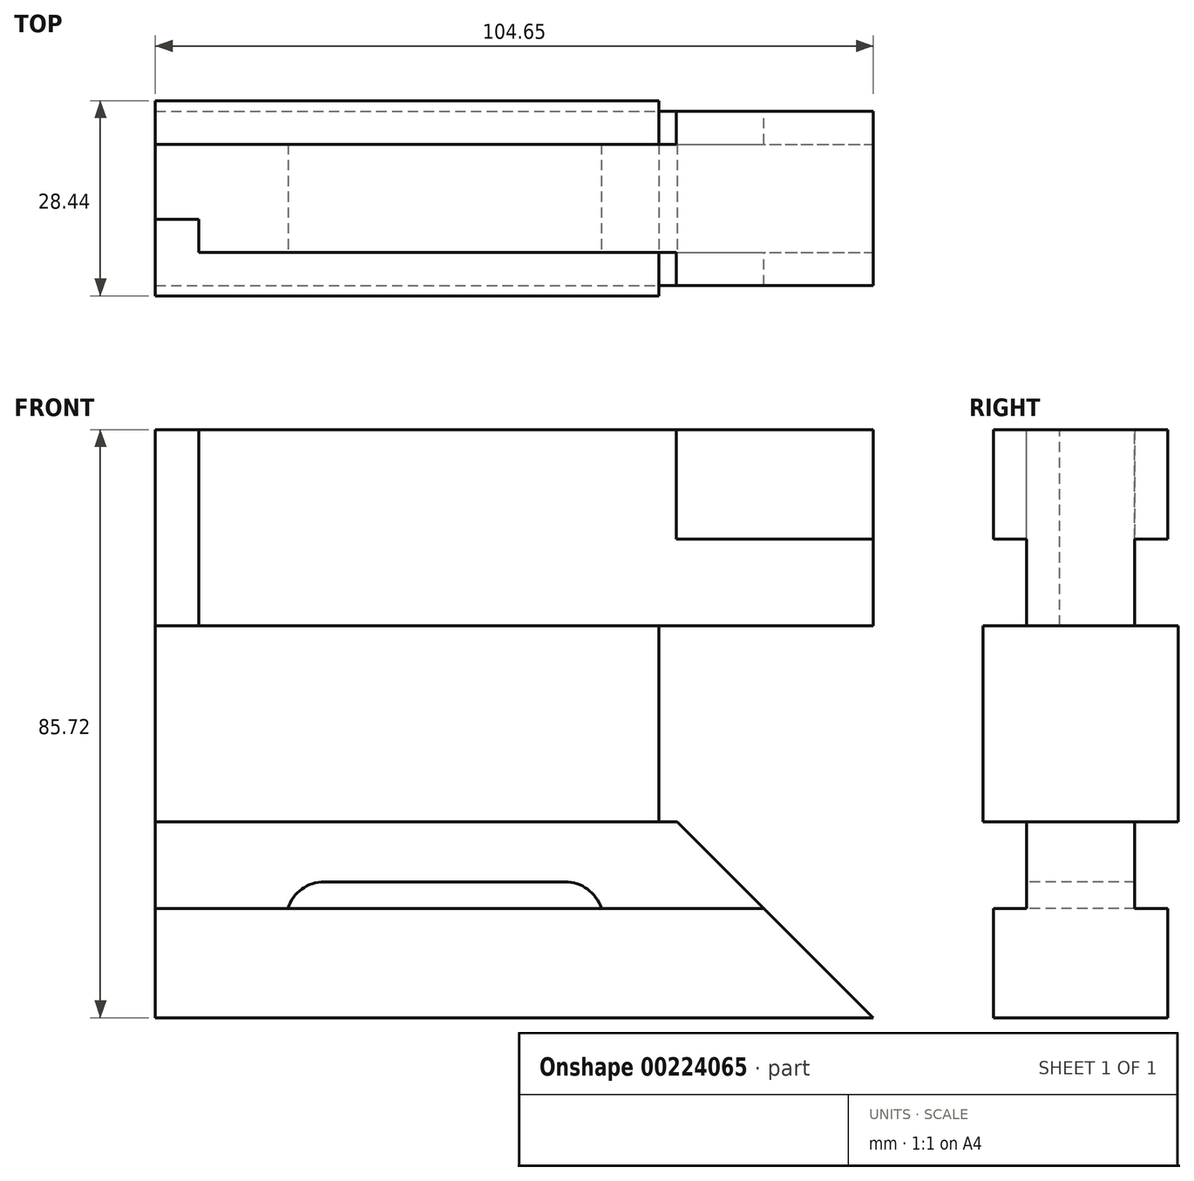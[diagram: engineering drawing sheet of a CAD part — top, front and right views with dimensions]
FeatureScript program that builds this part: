
annotation { "Feature Type Name" : "Feature", "Feature Type Description" : "" }
export const myFeature = defineFeature(function(context is Context, id is Id, definition is map)
    precondition{}
    {
        {
            var Q0;
            Q0=qCreatedBy(makeId("Right.planeOp"),FACE);
            var sketch = newSketch(context, id + "F0", { "sketchPlane" : qUnion([Q0])});
            skLineSegment(sketch, "E0.bottom", {"start": v(14.22, -14.29) * mm, "end": v(-14.22, -14.29) * mm});
            skLineSegment(sketch, "E0.top", {"start": v(14.22, 14.29) * mm, "end": v(-14.22, 14.29) * mm});
            skLineSegment(sketch, "E0.left", {"start": v(14.22, -14.29) * mm, "end": v(14.22, 14.29) * mm});
            skLineSegment(sketch, "E0.right", {"start": v(-14.22, -14.29) * mm, "end": v(-14.22, 14.29) * mm});
            skPoint(sketch, "E0.middle", {"position": v(0, 0) * mm});
            skLineSegment(sketch, "E1", {"start": v(-14.22, 14.29) * mm, "end": v(-12.7, 14.29) * mm, "construction": true});
            skLineSegment(sketch, "E2", {"start": v(0, 42.86) * mm, "end": v(-12.7, 42.86) * mm});
            skLineSegment(sketch, "E3", {"start": v(-12.7, 42.86) * mm, "end": v(-12.7, 26.92) * mm});
            skLineSegment(sketch, "E4.MirrorCS", {"start": v(0, 42.86) * mm, "end": v(12.7, 42.86) * mm});
            skLineSegment(sketch, "E5.MirrorCS", {"start": v(12.7, 42.86) * mm, "end": v(12.7, 26.92) * mm});
            skLineSegment(sketch, "E6", {"start": v(-12.7, 26.92) * mm, "end": v(-7.87, 26.92) * mm});
            skLineSegment(sketch, "E7", {"start": v(-7.87, 26.92) * mm, "end": v(-7.87, 14.29) * mm});
            skLineSegment(sketch, "E8.MirrorCS", {"start": v(12.7, 26.92) * mm, "end": v(7.87, 26.92) * mm});
            skLineSegment(sketch, "E9.MirrorCS", {"start": v(7.87, 26.92) * mm, "end": v(7.87, 14.29) * mm});
            skLineSegment(sketch, "E10.MirrorCS", {"start": v(-7.87, -26.92) * mm, "end": v(-7.87, -14.29) * mm});
            skLineSegment(sketch, "E11.MirrorCS", {"start": v(-12.7, -26.92) * mm, "end": v(-7.87, -26.92) * mm});
            skLineSegment(sketch, "E12.MirrorCS", {"start": v(-12.7, -42.86) * mm, "end": v(-12.7, -26.92) * mm});
            skLineSegment(sketch, "E13.MirrorCS", {"start": v(0, -42.86) * mm, "end": v(-12.7, -42.86) * mm});
            skLineSegment(sketch, "E14.MirrorCS", {"start": v(0, -42.86) * mm, "end": v(12.7, -42.86) * mm});
            skLineSegment(sketch, "E15.MirrorCS", {"start": v(12.7, -42.86) * mm, "end": v(12.7, -26.92) * mm});
            skLineSegment(sketch, "E16.MirrorCS", {"start": v(12.7, -26.92) * mm, "end": v(7.87, -26.92) * mm});
            skLineSegment(sketch, "E17.MirrorCS", {"start": v(7.87, -26.92) * mm, "end": v(7.87, -14.29) * mm});
            skSolve(sketch);
        }
        {
            var Q0;
            {var subQ0=sQuery(id+"F0.wireOp",EDGE,"E0.left");Q0=makeQuery(id+"F0.imprint","IMPRINT",FACE,{"disambiguationData":[TD([[makeQuery(id+"F0.imprint","IMPRINT",EDGE,{"derivedFrom":subQ0}),1.0]])]});}
            var Q1;
            Q1=makeQuery(id+"F0.imprint","IMPRINT",FACE,{"disambiguationData":[TD([[makeQuery(id+"F0.imprint","IMPRINT",EDGE,{"derivedFrom":sQuery(id+"F0.wireOp",EDGE,"E2")}),1.0]])]});
            var Q2;
            {var subQ0=sQuery(id+"F0.wireOp",EDGE,"E10.MirrorCS");Q2=makeQuery(id+"F0.imprint","IMPRINT",FACE,{"disambiguationData":[TD([[makeQuery(id+"F0.imprint","IMPRINT",EDGE,{"derivedFrom":subQ0}),-1.0]])]});}
            extrude(context, id + "F1", {"entities" : qUnion([Q0, Q1, Q2]), "oppositeDirection" : true, "depth" : 104.65 * mm});
        }
        {
            var Q0;
            Q0=makeQuery(id+"F1.opExtrude","SWEPT_FACE",FACE,{"disambiguationData":[OSD([sQuery(id+"F0.wireOp",EDGE,"E2"),sQuery(id+"F0.wireOp",EDGE,"E4.MirrorCS")])]});
            var sketch = newSketch(context, id + "F2", { "sketchPlane" : qUnion([Q0])});
            skPoint(sketch, "E18.0", {"position": v(-104.65, 14.22) * mm});
            skLineSegment(sketch, "E19.0", {"start": v(-104.65, 14.22) * mm, "end": v(0, 14.22) * mm, "construction": true});
            skLineSegment(sketch, "E20.0", {"start": v(-104.65, 14.22) * mm, "end": v(-104.65, 7.87) * mm, "construction": true});
            skLineSegment(sketch, "E21", {"start": v(-104.65, 14.22) * mm, "end": v(-104.65, 7.87) * mm});
            skLineSegment(sketch, "E22", {"start": v(-104.65, 7.87) * mm, "end": v(-104.65, -7.87) * mm});
            skLineSegment(sketch, "E23.MirrorCS", {"start": v(-104.65, -14.22) * mm, "end": v(-104.65, -7.87) * mm, "construction": true});
            skLineSegment(sketch, "E24.bottom", {"start": v(-104.65, -7.87) * mm, "end": v(-98.3, -7.87) * mm});
            skLineSegment(sketch, "E24.top", {"start": v(-104.65, -3.05) * mm, "end": v(-98.3, -3.05) * mm});
            skLineSegment(sketch, "E24.left", {"start": v(-104.65, -7.87) * mm, "end": v(-104.65, -3.05) * mm});
            skLineSegment(sketch, "E24.right", {"start": v(-98.3, -7.87) * mm, "end": v(-98.3, -3.05) * mm});
            skLineSegment(sketch, "E25", {"start": v(-98.3, -7.87) * mm, "end": v(-28.7, -7.87) * mm});
            skLineSegment(sketch, "E26", {"start": v(-104.65, 7.87) * mm, "end": v(-28.7, 7.87) * mm});
            skLineSegment(sketch, "E27", {"start": v(0, 12.7) * mm, "end": v(-28.7, 12.7) * mm});
            skLineSegment(sketch, "E28", {"start": v(-28.7, 12.7) * mm, "end": v(-28.7, 7.87) * mm});
            skLineSegment(sketch, "E29", {"start": v(0, 12.7) * mm, "end": v(0, -12.7) * mm});
            skLineSegment(sketch, "E30", {"start": v(0, -12.7) * mm, "end": v(-28.7, -12.7) * mm});
            skLineSegment(sketch, "E31", {"start": v(-28.7, -12.7) * mm, "end": v(-28.7, -7.87) * mm});
            skSolve(sketch);
        }
        {
            var Q0;
            {var subQ5=sQuery(id+"F2.wireOp",EDGE,"E24.bottom");Q0=makeQuery(id+"F2.imprint","IMPRINT",FACE,{"disambiguationData":[TD([[makeQuery(id+"F2.imprint","IMPRINT",EDGE,{"derivedFrom":subQ5}),-1.0]])]});}
            var Q1;
            {var subQ3=sQuery(id+"F2.wireOp",EDGE,"E26");Q1=makeQuery(id+"F2.imprint","IMPRINT",FACE,{"disambiguationData":[TD([[makeQuery(id+"F2.imprint","IMPRINT",EDGE,{"derivedFrom":subQ3}),1.0]])]});}
            var Q2;
            Q2=makeQuery(id+"F2.imprint","IMPRINT",FACE,{"disambiguationData":[TD([[makeQuery(id+"F2.imprint","IMPRINT",EDGE,{"derivedFrom":sQuery(id+"F2.wireOp",EDGE,"E24.bottom")}),1.0]])]});
            extrude(context, id + "F3", {"entities" : qUnion([Q0, Q1, Q2]), "operationType" : NewBodyOperationType.REMOVE, "oppositeDirection" : true, "depth" : 28.57 * mm});
        }
        {
            var Q0;
            Q0=makeQuery(id+"FJ5fPhw9AAkPfoI_1.1.F3.boolean.opBoolean","MERGE",FACE,{"derivedFrom":[makeQuery(id+"F1.opExtrude","SWEPT_FACE",FACE,{"disambiguationData":[OSD([sQuery(id+"F0.wireOp",EDGE,"E10.MirrorCS")])]}),makeQuery(id+"FJ5fPhw9AAkPfoI_1.1.F3.opExtrude","SWEPT_FACE",FACE,{"disambiguationData":[OSD([sQuery(id+"F2.wireOp",EDGE,"E25")])]})]});
            var sketch = newSketch(context, id + "F4", { "sketchPlane" : qUnion([Q0])});
            skPoint(sketch, "E32.0", {"position": v(-104.65, -42.86) * mm});
            skLineSegment(sketch, "E33", {"start": v(-104.65, -42.86) * mm, "end": v(-80.01, -42.86) * mm, "construction": true});
            skLineSegment(sketch, "E34", {"start": v(-80.01, -42.86) * mm, "end": v(-80.01, -28.64) * mm, "construction": true});
            skCircle(sketch, "E35", {"center": v(-80.01, -28.64) * mm, "radius": 5.59 * mm});
            skCircle(sketch, "E36", {"center": v(-44.96, -28.64) * mm, "radius": 5.59 * mm});
            skLineSegment(sketch, "E37", {"start": v(-80.01, -23.05) * mm, "end": v(-44.96, -23.05) * mm});
            skLineSegment(sketch, "E38", {"start": v(-44.96, -34.23) * mm, "end": v(-80.01, -34.23) * mm});
            skSolve(sketch);
        }
        {
            var Q0;
            {var subQ0=sQuery(id+"F4.wireOp",EDGE,"E35");var subQ1=makeQuery(id+"F4.imprint","INTERSECT",VERTEX,{"derivedFrom":[subQ0,sQuery(id+"F4.wireOp",EDGE,"E37")]});Q0=makeQuery(id+"F4.imprint","IMPRINT",FACE,{"disambiguationData":[TD([[makeQuery(id+"F4.imprint","IMPRINT",EDGE,{"disambiguationData":[TD([[subQ1,-1.0]])],"derivedFrom":subQ0}),1.0]])]});}
            var Q1;
            {var subQ0=sQuery(id+"F4.wireOp",EDGE,"E37");Q1=makeQuery(id+"F4.imprint","IMPRINT",FACE,{"disambiguationData":[TD([[makeQuery(id+"F4.imprint","IMPRINT",EDGE,{"derivedFrom":subQ0}),-1.0]])]});}
            var Q2;
            {var subQ0=sQuery(id+"F4.wireOp",EDGE,"E36");var subQ1=makeQuery(id+"F4.imprint","INTERSECT",VERTEX,{"derivedFrom":[subQ0,sQuery(id+"F4.wireOp",EDGE,"E37")]});Q2=makeQuery(id+"F4.imprint","IMPRINT",FACE,{"disambiguationData":[TD([[makeQuery(id+"F4.imprint","IMPRINT",EDGE,{"disambiguationData":[TD([[subQ1,-1.0]])],"derivedFrom":subQ0}),1.0]])]});}
            extrude(context, id + "F5", {"entities" : qUnion([Q0, Q1, Q2]), "operationType" : NewBodyOperationType.REMOVE, "endBound" : BoundingType.THROUGH_ALL, "oppositeDirection" : true, "depth" : 25.4 * mm});
        }
        {
            var Q0;
            Q0=makeQuery(id+"F1.opExtrude","SWEPT_FACE",FACE,{"disambiguationData":[OSD([sQuery(id+"F0.wireOp",EDGE,"E12.MirrorCS")])]});
            var sketch = newSketch(context, id + "F6", { "sketchPlane" : qUnion([Q0])});
            skLineSegment(sketch, "E39.0", {"start": v(-104.65, -14.29) * mm, "end": v(0, -14.29) * mm});
            skLineSegment(sketch, "E40", {"start": v(0, -42.86) * mm, "end": v(-28.58, -14.29) * mm});
            skLineSegment(sketch, "E41", {"start": v(-28.58, -14.29) * mm, "end": v(0, -14.29) * mm});
            skLineSegment(sketch, "E42", {"start": v(0, -42.86) * mm, "end": v(0, -14.29) * mm});
            skSolve(sketch);
        }
        {
            var Q0;
            Q0 = qSketchRegion(id + "F6", true);
            extrude(context, id + "F7", {"entities" : qUnion([Q0]), "operationType" : NewBodyOperationType.REMOVE, "endBound" : BoundingType.THROUGH_ALL, "oppositeDirection" : true, "depth" : 25.4 * mm});
        }
        {
            var Q0;
            Q0=makeQuery(id+"F1.opExtrude","SWEPT_FACE",FACE,{"disambiguationData":[OSD([sQuery(id+"F0.wireOp",EDGE,"E0.right")])]});
            var sketch = newSketch(context, id + "F8", { "sketchPlane" : qUnion([Q0])});
            skLineSegment(sketch, "E43", {"start": v(-104.65, 0) * mm, "end": v(-31.24, 0) * mm, "construction": true});
            skLineSegment(sketch, "E44", {"start": v(-31.24, 0) * mm, "end": v(-31.24, 14.29) * mm});
            skLineSegment(sketch, "E45", {"start": v(-31.24, 14.29) * mm, "end": v(0, 14.29) * mm});
            skLineSegment(sketch, "E46", {"start": v(0, 14.29) * mm, "end": v(0, -14.29) * mm});
            skLineSegment(sketch, "E47", {"start": v(0, -14.29) * mm, "end": v(-31.24, -14.29) * mm});
            skLineSegment(sketch, "E48", {"start": v(-31.24, -14.29) * mm, "end": v(-31.24, 0) * mm});
            skSolve(sketch);
        }
        {
            var Q0;
            Q0 = qSketchRegion(id + "F8", true);
            extrude(context, id + "F9", {"entities" : qUnion([Q0]), "operationType" : NewBodyOperationType.REMOVE, "endBound" : BoundingType.THROUGH_ALL, "oppositeDirection" : true, "depth" : 25.4 * mm});
        }
    });
